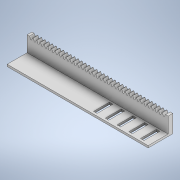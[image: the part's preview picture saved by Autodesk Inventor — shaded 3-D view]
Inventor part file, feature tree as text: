
AUTODESK INVENTOR PART (.ipt)
format: ipt  version: 2020 (Build 240168000, 168)  size: 331,264 bytes
history: native  units: mm
features: sketch x4, extrude x4, pattern_linear x1
ambient origin geometry x8: Origin, YZ Plane, XZ Plane, XY Plane, X Axis, Y Axis, Z Axis, Center Point
bodies: Body1 (feature_tree)
feature tree (9):
  sketch  "Sketch1"  dims[d7=120.0mm d8=4.0mm]
  extrude  "Extrusion3"  Depth=4.0mm
  extrude  "Extrusion4"  Depth=2.0mm TaperAngle=0.0deg
  pattern_linear  "Rectangular Pattern1"  Count1=37 Spacing1=3.141593mm
  extrude  "Extrusion5"  Depth=17.0mm
  extrude  "Extrusion6"  Depth=1.75mm
  sketch  "Sketch2"  dims[d9=2.0mm d10=4.0mm d11=0.0mm]
  sketch  "Sketch3"  dims[d12=4.0mm d13=0.0mm d14=370.0mm d16=3.141593mm]
  sketch  "Sketch4"  dims[d17=11.0mm d18=17.0mm d19=1.75mm d20=120.0mm d21=0.0mm d22=2.0mm d24=3.0mm d25=60.0mm d27=20.0mm d28=10.0mm d30=10.0mm d32=120.0mm d33=0.0mm d34=50.0mm d36=10.0mm d37=10.0mm d39=10.0mm]
